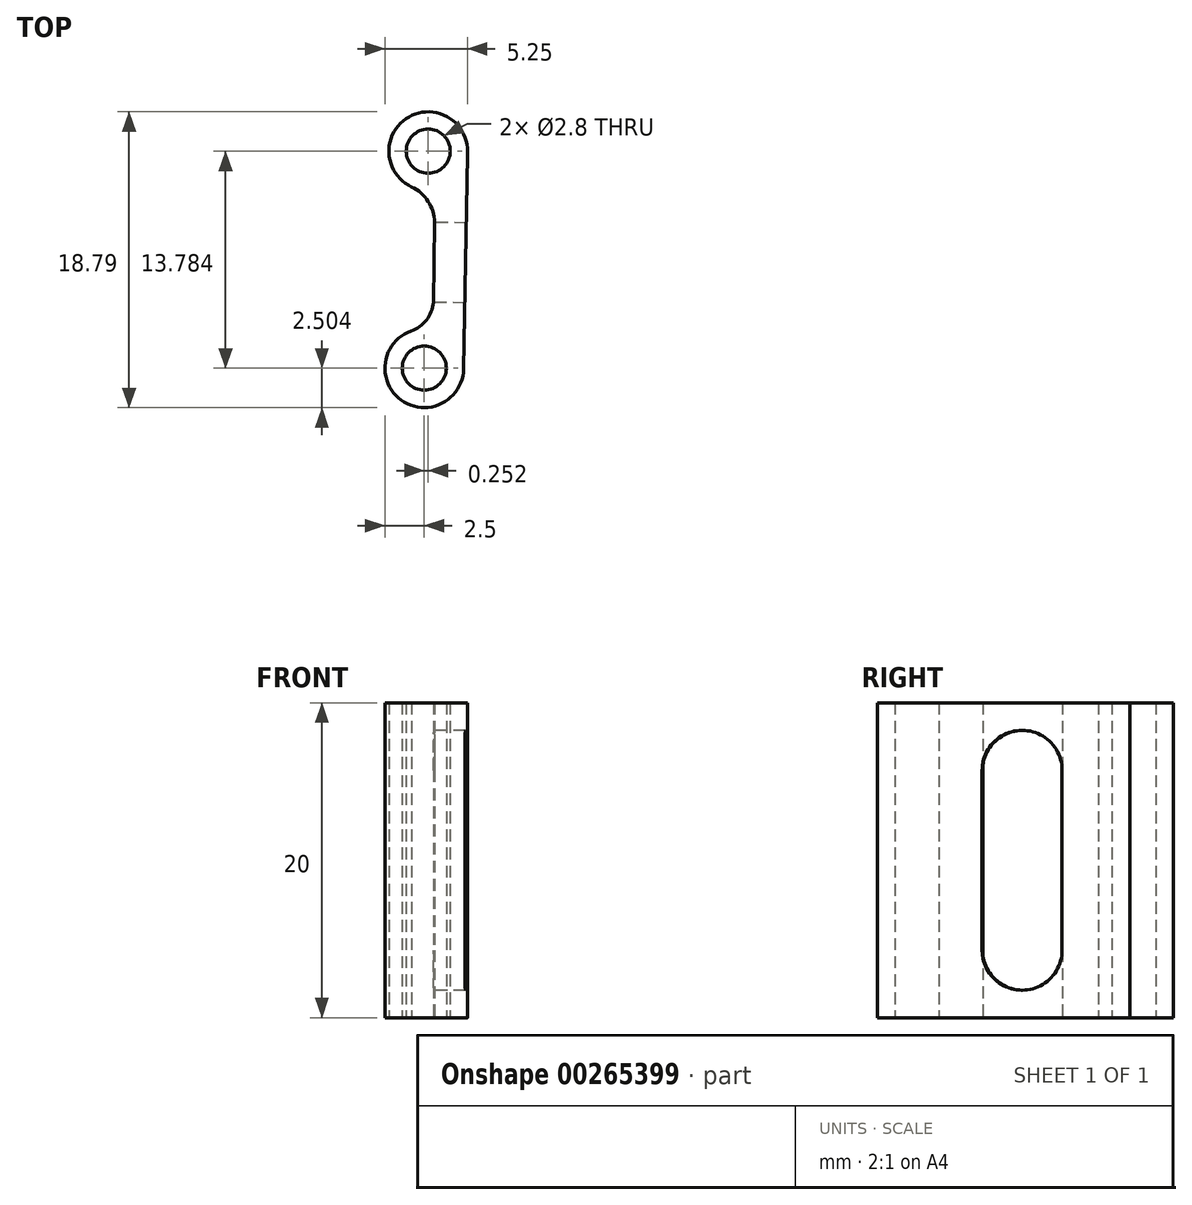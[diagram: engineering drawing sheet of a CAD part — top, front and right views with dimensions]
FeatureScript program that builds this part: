
annotation { "Feature Type Name" : "Feature", "Feature Type Description" : "" }
export const myFeature = defineFeature(function(context is Context, id is Id, definition is map)
    precondition{}
    {
        {
            var Q0;
            Q0=qCreatedBy(makeId("Top.planeOp"),FACE);
            var sketch = newSketch(context, id + "F0", { "sketchPlane" : qUnion([Q0])});
            skCircle(sketch, "E0", {"center": v(-9.25, 3.82) * mm, "radius": 1.4 * mm});
            skCircle(sketch, "E1", {"center": v(-9.5, -9.97) * mm, "radius": 1.4 * mm});
            skArc(sketch, "E2", {"start": v(-6.76, 3.55) * mm, "mid": v(-10.48, 6) * mm, "end": v(-10.3, 1.55) * mm});
            skArc(sketch, "E3", {"start": v(-10.33, -7.6) * mm, "mid": v(-10.96, -12) * mm, "end": v(-7, -10) * mm});
            skLineSegment(sketch, "E4", {"start": v(-6.76, 3.55) * mm, "end": v(-7, -10) * mm});
            skLineSegment(sketch, "E5.0", {"start": v(-8.84, -0.7) * mm, "end": v(-8.93, -5.78) * mm});
            skArc(sketch, "E6", {"start": v(-8.84, -0.98) * mm, "mid": v(-9.2, 0.53) * mm, "end": v(-10.35, 1.57) * mm});
            skArc(sketch, "E7", {"start": v(-10.35, -7.61) * mm, "mid": v(-9.28, -6.79) * mm, "end": v(-8.92, -5.48) * mm});
            skSolve(sketch);
        }
        {
            var Q0;
            Q0 = qSketchRegion(id + "F0", true);
            extrude(context, id + "F1", {"entities" : qUnion([Q0]), "depth" : 20 * mm});
        }
        {
            var Q0;
            Q0=makeQuery(id+"F1.opExtrude","SWEPT_FACE",FACE,{"disambiguationData":[OSD([sQuery(id+"F0.wireOp",EDGE,"E5.0")])]});
            var sketch = newSketch(context, id + "F2", { "sketchPlane" : qUnion([Q0])});
            skLineSegment(sketch, "E8", {"start": v(3.4, 20) * mm, "end": v(3.4, 0) * mm, "construction": true});
            skLineSegment(sketch, "E9", {"start": v(0.86, 10) * mm, "end": v(5.94, 10) * mm, "construction": true});
            skLineSegment(sketch, "E10.bottom", {"start": v(5.94, 15.71) * mm, "end": v(0.86, 15.71) * mm, "construction": true});
            skLineSegment(sketch, "E10.top", {"start": v(5.94, 4.29) * mm, "end": v(0.86, 4.29) * mm, "construction": true});
            skLineSegment(sketch, "E10.left", {"start": v(5.94, 15.71) * mm, "end": v(5.94, 4.29) * mm});
            skLineSegment(sketch, "E10.right", {"start": v(0.86, 15.71) * mm, "end": v(0.86, 4.29) * mm});
            skPoint(sketch, "E10.middle", {"position": v(3.4, 10) * mm});
            skArc(sketch, "E11", {"start": v(5.94, 15.71) * mm, "mid": v(3.4, 18.25) * mm, "end": v(0.86, 15.71) * mm});
            skArc(sketch, "E12.MirrorCS", {"start": v(5.94, 4.29) * mm, "mid": v(3.4, 1.75) * mm, "end": v(0.86, 4.29) * mm});
            skSolve(sketch);
        }
        {
            var Q0;
            Q0=makeQuery(id+"F2.imprint","IMPRINT",FACE,{"disambiguationData":[TD([[makeQuery(id+"F2.imprint","IMPRINT",EDGE,{"derivedFrom":sQuery(id+"F2.wireOp",EDGE,"E10.left")}),-1.0]])]});
            extrude(context, id + "F3", {"entities" : qUnion([Q0]), "operationType" : NewBodyOperationType.REMOVE, "oppositeDirection" : true, "depth" : 25 * mm, "offsetDistance" : 25 * mm});
        }
    });
